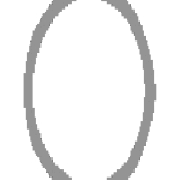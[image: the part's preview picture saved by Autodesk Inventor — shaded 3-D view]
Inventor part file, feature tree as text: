
AUTODESK INVENTOR PART (.ipt)
format: ipt  version: 2021 (Build 250183000, 183)  size: 110,080 bytes
history: native  units: in
note: dims shown in document units (in); Inventor stores cm internally (conversion verified against a paired STEP export)
features: other x4, sketch x3, plane x1
ambient origin geometry x8: Origin, YZ Plane, XZ Plane, XY Plane, X Axis, Y Axis, Z Axis, Center Point
bodies: Solid1 (feature_tree), Body (feature_tree)
feature tree (8):
  other  "Driven Length"
  other  "Frame Generator"
  other  "Start Plane"
  other  "End Plane"
  sketch  "Sketch"  dims[d2=12.0in d4=-0.0in d5=12.0in d6=0.12in d7=0.0in d8=90.0deg d9=12.0in]
  sketch  "Sketch2"  dims[d0=1.0in]
  plane  "Work Plane3"
  sketch  "Sketch3"  dims[d1=0.065in]
